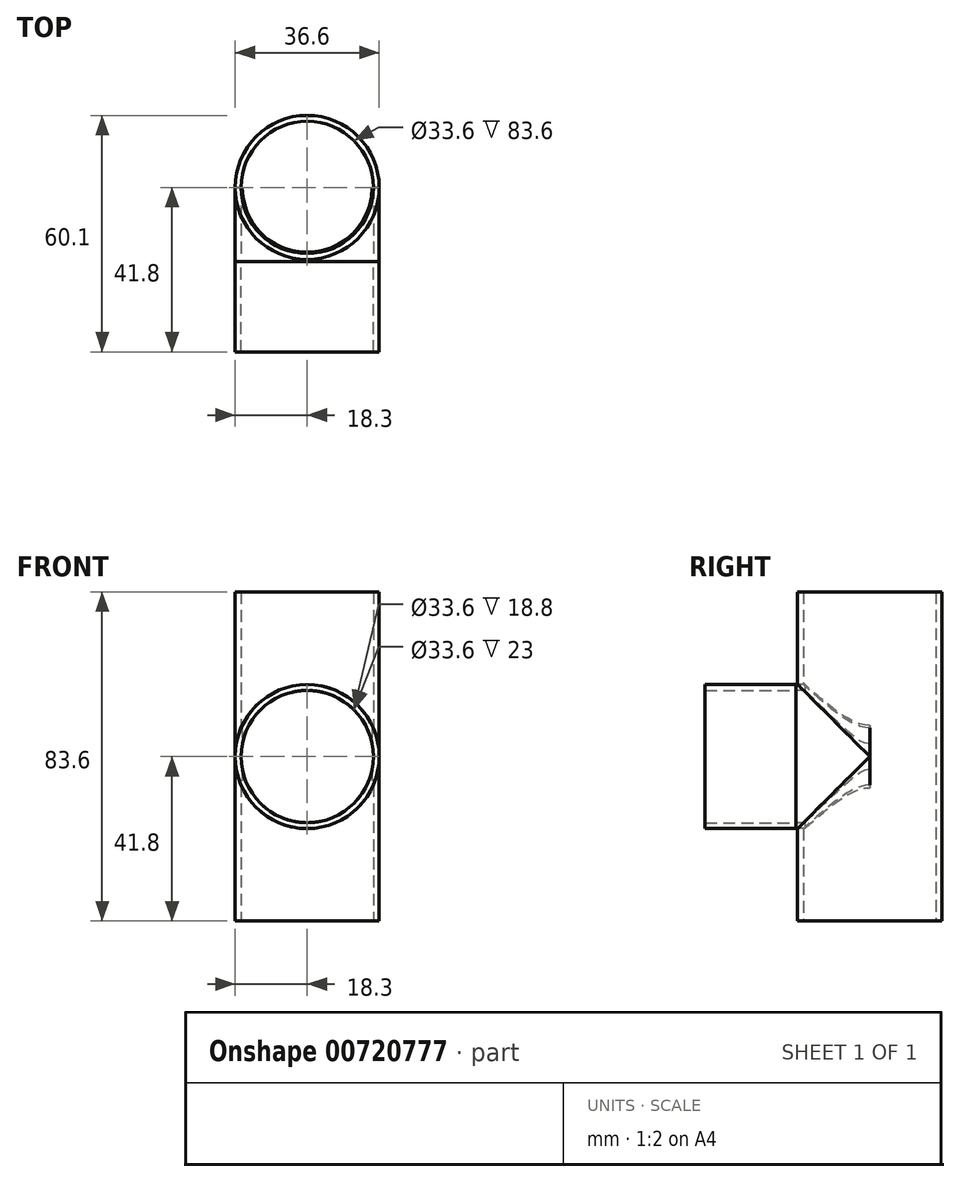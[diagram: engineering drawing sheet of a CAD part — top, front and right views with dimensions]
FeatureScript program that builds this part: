
annotation { "Feature Type Name" : "Feature", "Feature Type Description" : "" }
export const myFeature = defineFeature(function(context is Context, id is Id, definition is map)
    precondition{}
    {
        {
            var Q0;
            Q0=qCreatedBy(makeId("Top.planeOp"),FACE);
            var sketch = newSketch(context, id + "F0", { "sketchPlane" : qUnion([Q0])});
            skCircle(sketch, "E0", {"center": v(0, 0) * mm, "radius": 16.8 * mm});
            skCircle(sketch, "E1", {"center": v(0, 0) * mm, "radius": 16.3 * mm});
            skCircle(sketch, "E2", {"center": v(0, 0) * mm, "radius": 18.3 * mm});
            skSolve(sketch);
        }
        {
            var Q0;
            Q0=qSketchRegion(id+"F0",true);
            extrude(context, id + "F1", {"entities" : qUnion([Q0]), "depth" : 83.6 * mm, "offsetDistance" : 25 * mm});
        }
        {
            var Q0;
            Q0=qCreatedBy(makeId("Front.planeOp"),FACE);
            cPlane(context, id + "F2", {"entities" : qUnion([Q0]), "cplaneType" : CPlaneType.OFFSET, "offset" : 18.8 * mm, "width" : 150 * mm, "height" : 150 * mm});
        }
        {
            var Q0;
            Q0=qCreatedBy(id+"F2.planeOp",FACE);
            var sketch = newSketch(context, id + "F3", { "sketchPlane" : qUnion([Q0])});
            skLineSegment(sketch, "E3", {"start": v(0, 0) * mm, "end": v(0, 23) * mm, "construction": true});
            skLineSegment(sketch, "E4", {"start": v(0, 23) * mm, "end": v(0, 41.8) * mm, "construction": true});
            skCircle(sketch, "E5", {"center": v(0, 41.8) * mm, "radius": 18.3 * mm});
            skCircle(sketch, "E6", {"center": v(0, 41.8) * mm, "radius": 16.8 * mm});
            skSolve(sketch);
        }
        {
            var Q0;
            Q0=makeQuery(id+"F3.imprint","IMPRINT",FACE,{"disambiguationData":[TD([[makeQuery(id+"F3.imprint","IMPRINT",EDGE,{"derivedFrom":sQuery(id+"F3.wireOp",EDGE,"E5")}),1.0]])]});
            extrude(context, id + "F4", {"entities" : qUnion([Q0]), "operationType" : NewBodyOperationType.ADD, "depth" : 23 * mm, "offsetDistance" : 25 * mm});
        }
        {
            var Q0;
            Q0=makeQuery(id+"F3.imprint","IMPRINT",FACE,{"disambiguationData":[TD([[makeQuery(id+"F3.imprint","IMPRINT",EDGE,{"derivedFrom":sQuery(id+"F3.wireOp",EDGE,"E5")}),1.0]])]});
            var Q1;
            Q1=makeQuery(id+"F3.imprint","IMPRINT",FACE,{"disambiguationData":[TD([[makeQuery(id+"F3.imprint","IMPRINT",EDGE,{"derivedFrom":sQuery(id+"F3.wireOp",EDGE,"E6")}),1.0]])]});
            extrude(context, id + "F5", {"entities" : qUnion([Q0, Q1]), "operationType" : NewBodyOperationType.REMOVE, "oppositeDirection" : true, "depth" : 18.8 * mm, "offsetDistance" : 25 * mm});
        }
        {
            var Q0;
            Q0=makeQuery(id+"F4.opExtrude","CAP_FACE",FACE,{"disambiguationData":[OSD([sQuery(id+"F3.wireOp",EDGE,"E5"),sQuery(id+"F3.wireOp",EDGE,"E6")])],"isStart":true});
            var sketch = newSketch(context, id + "F6", { "sketchPlane" : qUnion([Q0])});
            skSolve(sketch);
        }
        {
            var Q0;
            Q0=makeQuery(id+"F6.imprint","IMPRINT",FACE,{"disambiguationData":[TD([[makeQuery(id+"F6.imprint","IMPRINT",EDGE,{"derivedFrom":makeQuery(id+"F4.opExtrude","CAP_EDGE",EDGE,{"disambiguationData":[OSD([sQuery(id+"F3.wireOp",EDGE,"E5")])],"isStart":true})}),-1.0]])]});
            extrude(context, id + "F7", {"entities" : qUnion([Q0]), "depth" : 18.8 * mm, "offsetDistance" : 25 * mm});
        }
        {
            var Q0;
            Q0=makeQuery(id+"F1.opExtrude","CAP_FACE",FACE,{"disambiguationData":[OSD([sQuery(id+"F0.wireOp",EDGE,"E0"),sQuery(id+"F0.wireOp",EDGE,"E2")])],"isStart":true});
            var sketch = newSketch(context, id + "F8", { "sketchPlane" : qUnion([Q0])});
            skCircle(sketch, "E7", {"center": v(0, 0) * mm, "radius": 16.5 * mm});
            skSolve(sketch);
        }
        {
            var Q0;
            Q0=makeQuery(id+"F8.imprint","IMPRINT",FACE,{"disambiguationData":[TD([[makeQuery(id+"F8.imprint","IMPRINT",EDGE,{"derivedFrom":sQuery(id+"F8.wireOp",EDGE,"E7")}),1.0]])]});
            extrude(context, id + "F9", {"entities" : qUnion([Q0]), "operationType" : NewBodyOperationType.REMOVE, "oppositeDirection" : true, "depth" : 102.5 * mm, "offsetDistance" : 25 * mm});
        }
    });
